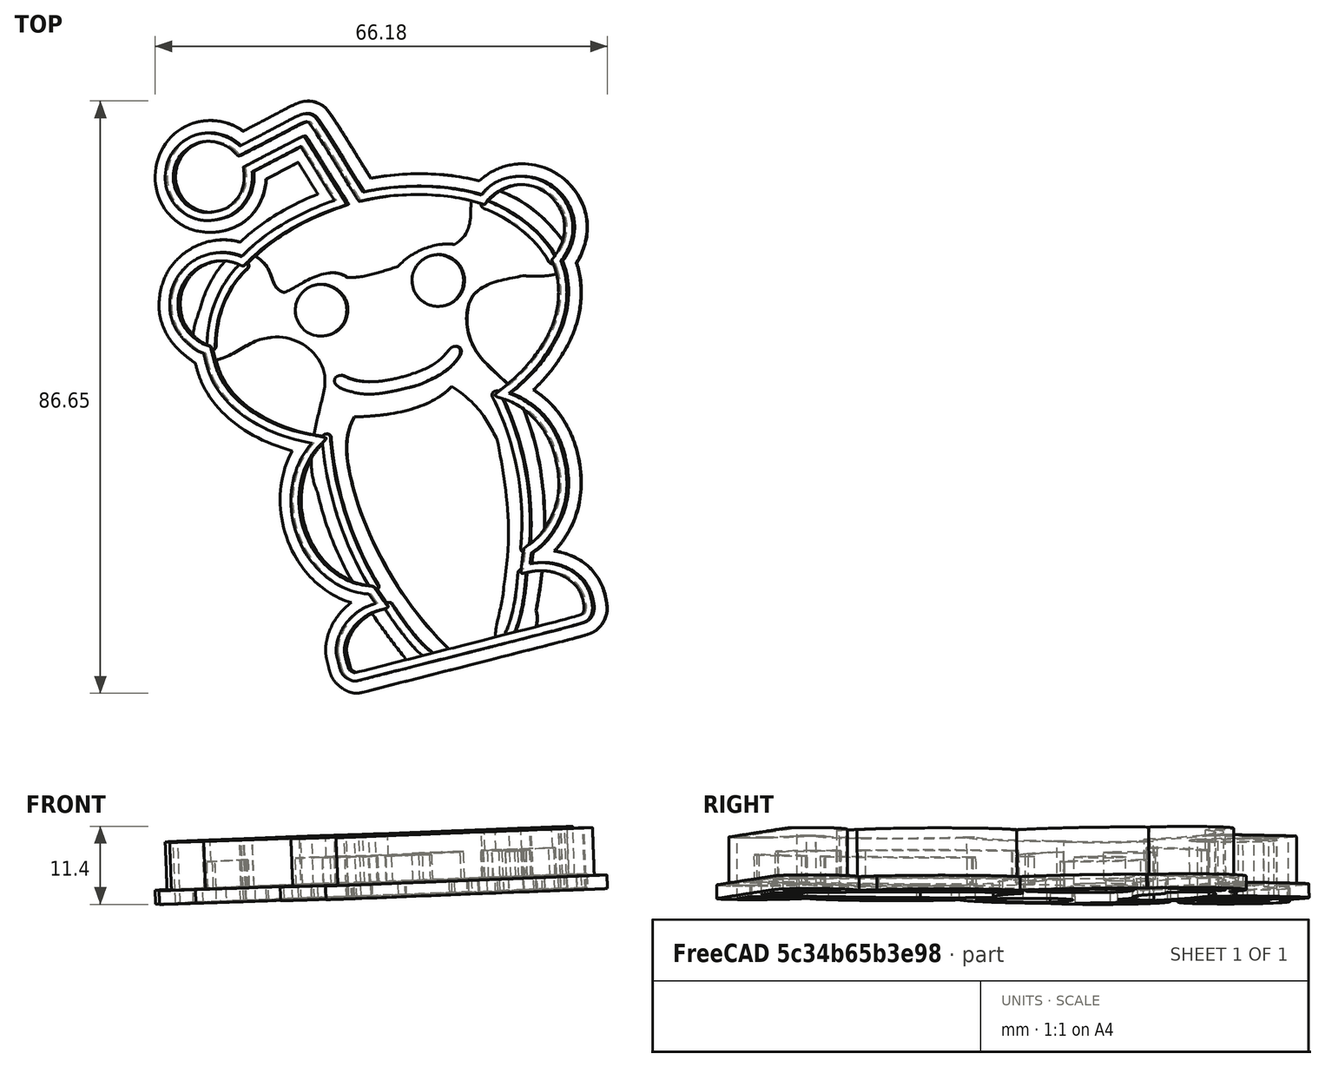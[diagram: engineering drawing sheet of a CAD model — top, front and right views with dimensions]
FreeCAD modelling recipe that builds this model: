
FCSTD DOCUMENT  (FreeCAD 0.19R)
Label: snoocutter
License: All rights reserved
LicenseURL: http://en.wikipedia.org/wiki/All_rights_reserved
objects: Part::Feature×24, Part::Extrusion×13, Part::MultiFuse×3, Part::Cut×2, App::DocumentObjectGroup×1, Spreadsheet::Sheet×1, Part::Mirroring×1
note: 43 computed .brp shape members not serialized (recipe doc carries the construction recipe); baked Part::Feature solids carry a one-line shape summary decoded from their .brp

FEATURE [Part::Feature] path1118  label="outer base"
  shape: bbox 64.33 x 86.82 x 2e-07 mm, 0 faces, 0 solids (baked)
FEATURE [Part::Feature] path1118004  label="base cutout"
  shape: bbox 41.68 x 25.02 x 2e-07 mm, 0 faces, 0 solids (baked)
FEATURE [Part::Feature] path1118005
  shape: bbox 8.44 x 9.882 x 2e-07 mm, 0 faces, 0 solids (baked)
FEATURE [Part::Feature] path1118006
  shape: bbox 8.388 x 9.659 x 2e-07 mm, 0 faces, 0 solids (baked)
FEATURE [Part::Feature] path1118007
  shape: bbox 15.5 x 15.46 x 2e-07 mm, 0 faces, 0 solids (baked)
FEATURE [Part::Feature] path1118008
  shape: bbox 15.15 x 15.1 x 2e-07 mm, 0 faces, 0 solids (baked)
FEATURE [Part::Feature] path1118009
  shape: bbox 12.91 x 8.505 x 2e-07 mm, 0 faces, 0 solids (baked)
FEATURE [Part::Feature] path1118010
  shape: bbox 22.23 x 37.16 x 2e-07 mm, 0 faces, 0 solids (baked)
FEATURE [Part::Feature] path1118011
  shape: bbox 5.014 x 18.86 x 2e-07 mm, 0 faces, 0 solids (baked)
FEATURE [Part::Feature] path1118012
  shape: bbox 4.524 x 18.33 x 2e-07 mm, 0 faces, 0 solids (baked)
FEATURE [Part::Feature] path1118013
  shape: bbox 8.251 x 7.847 x 2e-07 mm, 0 faces, 0 solids (baked)
FEATURE [Part::Feature] path1118014
  shape: bbox 8.09 x 7.809 x 2e-07 mm, 0 faces, 0 solids (baked)
FEATURE [Part::Feature] path940  label="cutter out"
  shape: bbox 60.68 x 83.24 x 2e-07 mm, 0 faces, 0 solids (baked)
FEATURE [Part::Feature] path860  label="cutter in"
  shape: bbox 58.24 x 81 x 2e-07 mm, 0 faces, 0 solids (baked)
FEATURE [Part::Feature] path990  label="mouth"
  shape: bbox 19.24 x 4.227 x 2e-07 mm, 0 faces, 0 solids (baked)
FEATURE [Part::Feature] path992  label="eye"
  shape: bbox 7.733 x 7.802 x 2e-07 mm, 0 faces, 0 solids (baked)
FEATURE [Part::Feature] path994  label="eye001"
  shape: bbox 7.95 x 7.792 x 2e-07 mm, 0 faces, 0 solids (baked)
FEATURE [Part::Feature] path996  label="ear"
  shape: bbox 9.014 x 11.6 x 2e-07 mm, 0 faces, 0 solids (baked)
FEATURE [Part::Feature] path998  label="ear001"
  shape: bbox 8.871 x 11.47 x 2e-07 mm, 0 faces, 0 solids (baked)
FEATURE [Part::Feature] path1000  label="arm"
  shape: bbox 4.802 x 24.12 x 2e-07 mm, 0 faces, 0 solids (baked)
FEATURE [Part::Feature] path1002  label="arm001"
  shape: bbox 4.556 x 24.07 x 2e-07 mm, 0 faces, 0 solids (baked)
FEATURE [Part::Feature] path1004  label="foot"
  shape: bbox 5.324 x 9.366 x 2e-07 mm, 0 faces, 0 solids (baked)
FEATURE [Part::Feature] path1006  label="foot001"
  shape: bbox 5.202 x 9.435 x 2e-07 mm, 0 faces, 0 solids (baked)
FEATURE [App::DocumentObjectGroup] Group  label="details"
  Group = -> [path990,path992,path994,path996,path998,path1000,path1002,path1004,path1006]
FEATURE [Part::Feature] Wire
  shape: bbox 57.69 x 68.17 x 2e-07 mm, 0 faces, 0 solids (baked)
FEATURE [Spreadsheet::Sheet] Spreadsheet
  cells = A1=base t; B1=2; A2=cutter height; B2=7; A3=details height; B3=4
FEATURE [Part::Extrusion] Extrude  label="base"
  Base = -> path1118
  Dir = (0,0,1)
  DirMode = 2
  FaceMakerClass = Part::FaceMakerBullseye
  LengthFwd = 2
  LengthRev = 0
  Solid = true
  Symmetric = false
  expr: LengthFwd = Spreadsheet.B1
FEATURE [Part::Extrusion] Extrude002  label="cutter in001"
  Base = -> path860
  Dir = (0,0,-1)
  DirMode = 2
  FaceMakerClass = Part::FaceMakerBullseye
  LengthFwd = 9
  LengthRev = 0
  Reversed = true
  Solid = true
  Symmetric = false
  expr: LengthFwd = Spreadsheet.B2 + Spreadsheet.B1
FEATURE [Part::Extrusion] Extrude003  label="cutter out001"
  Base = -> path940
  Dir = (0,0,1)
  DirMode = 2
  FaceMakerClass = Part::FaceMakerBullseye
  LengthFwd = 9
  LengthRev = 0
  Solid = true
  Symmetric = false
  expr: LengthFwd = Spreadsheet.B2 + Spreadsheet.B1
FEATURE [Part::Cut] Cut  label="countour cutter"
  Base = -> Extrude003
  Tool = -> Extrude002
FEATURE [Part::Extrusion] Extrude004  label="details base"
  Base = -> Wire
  Dir = (0,0,1)
  DirMode = 2
  FaceMakerClass = Part::FaceMakerBullseye
  LengthFwd = 2
  LengthRev = 0
  Solid = true
  Symmetric = false
  expr: LengthFwd = Spreadsheet.B1
FEATURE [Part::Cut] Cut001  label="base countour"
  Base = -> Extrude
  Tool = -> Extrude002
FEATURE [Part::MultiFuse] Fusion
  Shapes = -> [Cut001,Extrude004]
FEATURE [Part::MultiFuse] Fusion001
  Shapes = -> [Cut,Fusion]
FEATURE [Part::Extrusion] Extrude005
  Base = -> path990
  Dir = (0,0,-1)
  DirMode = 2
  FaceMakerClass = Part::FaceMakerBullseye
  LengthFwd = 6
  LengthRev = 0
  Reversed = true
  Solid = true
  Symmetric = false
  expr: LengthFwd = Spreadsheet.B1 + Spreadsheet.B3
FEATURE [Part::Extrusion] Extrude006
  Base = -> path992
  Dir = (0,0,-1)
  DirMode = 2
  FaceMakerClass = Part::FaceMakerBullseye
  LengthFwd = 6
  LengthRev = 0
  Reversed = true
  Solid = true
  Symmetric = false
  expr: LengthFwd = Spreadsheet.B1 + Spreadsheet.B3
FEATURE [Part::Extrusion] Extrude007
  Base = -> path994
  Dir = (0,0,-1)
  DirMode = 2
  FaceMakerClass = Part::FaceMakerBullseye
  LengthFwd = 6
  LengthRev = 0
  Reversed = true
  Solid = true
  Symmetric = false
  expr: LengthFwd = Spreadsheet.B1 + Spreadsheet.B3
FEATURE [Part::Extrusion] Extrude008
  Base = -> path996
  Dir = (0,0,1)
  DirMode = 2
  FaceMakerClass = Part::FaceMakerBullseye
  LengthFwd = 6
  LengthRev = 0
  Solid = true
  Symmetric = false
  expr: LengthFwd = Spreadsheet.B1 + Spreadsheet.B3
FEATURE [Part::Extrusion] Extrude009
  Base = -> path998
  Dir = (0,0,1)
  DirMode = 2
  FaceMakerClass = Part::FaceMakerBullseye
  LengthFwd = 6
  LengthRev = 0
  Solid = true
  Symmetric = false
  expr: LengthFwd = Spreadsheet.B1 + Spreadsheet.B3
FEATURE [Part::Extrusion] Extrude010
  Base = -> path1000
  Dir = (0,0,1)
  DirMode = 2
  FaceMakerClass = Part::FaceMakerBullseye
  LengthFwd = 6
  LengthRev = 0
  Solid = true
  Symmetric = false
  expr: LengthFwd = Spreadsheet.B1 + Spreadsheet.B3
FEATURE [Part::Extrusion] Extrude011
  Base = -> path1002
  Dir = (0,0,1)
  DirMode = 2
  FaceMakerClass = Part::FaceMakerBullseye
  LengthFwd = 6
  LengthRev = 0
  Solid = true
  Symmetric = false
  expr: LengthFwd = Spreadsheet.B1 + Spreadsheet.B3
FEATURE [Part::Extrusion] Extrude012
  Base = -> path1004
  Dir = (0,0,1)
  DirMode = 2
  FaceMakerClass = Part::FaceMakerBullseye
  LengthFwd = 6
  LengthRev = 0
  Solid = true
  Symmetric = false
  expr: LengthFwd = Spreadsheet.B1 + Spreadsheet.B3
FEATURE [Part::Extrusion] Extrude013
  Base = -> path1006
  Dir = (0,0,1)
  DirMode = 2
  FaceMakerClass = Part::FaceMakerBullseye
  LengthFwd = 6
  LengthRev = 0
  Solid = true
  Symmetric = false
  expr: LengthFwd = Spreadsheet.B1 + Spreadsheet.B3
FEATURE [Part::MultiFuse] Fusion002
  Shapes = -> [Fusion001,Extrude005,Extrude006,Extrude007,Extrude008,Extrude009,Extrude010,Extrude011,Extrude012,Extrude013]
FEATURE [Part::Mirroring] mirror  label="Mirror of Fusion002"
  Base = (0,1,1)
  Normal = (0.992085,0.124045,0.019476)
  Source = -> Fusion002
